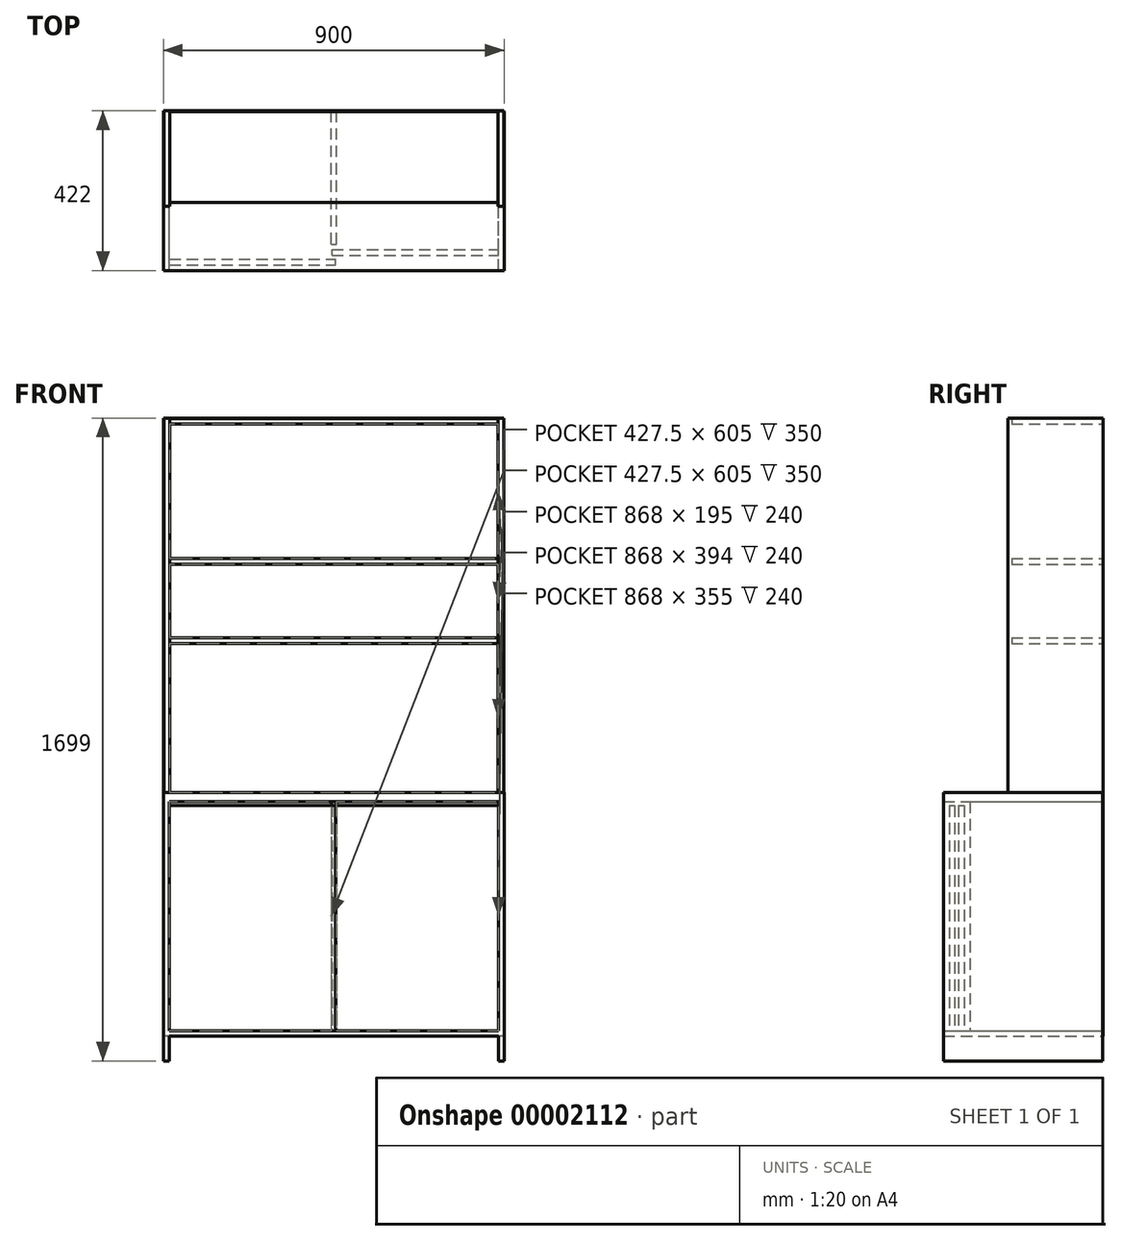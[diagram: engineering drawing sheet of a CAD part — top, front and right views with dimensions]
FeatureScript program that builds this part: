
annotation { "Feature Type Name" : "Feature", "Feature Type Description" : "" }
export const myFeature = defineFeature(function(context is Context, id is Id, definition is map)
    precondition{}
    {
        {
            var Q0;
            Q0=qCreatedBy(makeId("Top.planeOp"),FACE);
            var sketch = newSketch(context, id + "F0", { "sketchPlane" : qUnion([Q0])});
            skLineSegment(sketch, "E0.bottom", {"start": v(0, 0) * mm, "end": v(900, 0) * mm});
            skLineSegment(sketch, "E0.top", {"start": v(0, -420) * mm, "end": v(900, -420) * mm});
            skLineSegment(sketch, "E0.left", {"start": v(0, 0) * mm, "end": v(0, -420) * mm});
            skLineSegment(sketch, "E0.right", {"start": v(900, 0) * mm, "end": v(900, -420) * mm});
            skSolve(sketch);
        }
        {
            var Q0;
            Q0 = qSketchRegion(id + "F0", true);
            extrude(context, id + "F1", {"entities" : qUnion([Q0]), "flatOperationType" : FlatOperationType.REMOVE, "depth" : 24 * mm, "offsetDistance" : 25 * mm, "domain" : OperationDomain.MODEL});
        }
        {
            var Q0;
            Q0=makeQuery(id+"F1.opExtrude","CAP_FACE",FACE,{"disambiguationData":[OSD([sQuery(id+"F0.wireOp",EDGE,"E0.bottom"),sQuery(id+"F0.wireOp",EDGE,"E0.top"),sQuery(id+"F0.wireOp",EDGE,"E0.left"),sQuery(id+"F0.wireOp",EDGE,"E0.right")])],"isStart":true});
            var sketch = newSketch(context, id + "F2", { "sketchPlane" : qUnion([Q0])});
            skLineSegment(sketch, "E1.bottom", {"start": v(0, 420) * mm, "end": v(15, 420) * mm});
            skLineSegment(sketch, "E1.top", {"start": v(0, 0) * mm, "end": v(15, 0) * mm});
            skLineSegment(sketch, "E1.left", {"start": v(0, 420) * mm, "end": v(0, 0) * mm});
            skLineSegment(sketch, "E1.right", {"start": v(15, 420) * mm, "end": v(15, 0) * mm});
            skLineSegment(sketch, "E2.bottom", {"start": v(900, 420) * mm, "end": v(885, 420) * mm});
            skLineSegment(sketch, "E2.top", {"start": v(900, 0) * mm, "end": v(885, 0) * mm});
            skLineSegment(sketch, "E2.left", {"start": v(900, 420) * mm, "end": v(900, 0) * mm});
            skLineSegment(sketch, "E2.right", {"start": v(885, 420) * mm, "end": v(885, 0) * mm});
            skSolve(sketch);
        }
        {
            var Q0;
            Q0 = qSketchRegion(id + "F2", true);
            extrude(context, id + "F3", {"entities" : qUnion([Q0]), "operationType" : NewBodyOperationType.ADD, "depth" : 685 * mm});
        }
        {
            var Q0;
            Q0=makeQuery(id+"F1.opExtrude","CAP_FACE",FACE,{"disambiguationData":[OSD([sQuery(id+"F0.wireOp",EDGE,"E0.bottom"),sQuery(id+"F0.wireOp",EDGE,"E0.top"),sQuery(id+"F0.wireOp",EDGE,"E0.left"),sQuery(id+"F0.wireOp",EDGE,"E0.right")])],"isStart":false});
            var sketch = newSketch(context, id + "F4", { "sketchPlane" : qUnion([Q0])});
            skLineSegment(sketch, "E3.bottom", {"start": v(1, 0) * mm, "end": v(16, 0) * mm});
            skLineSegment(sketch, "E3.top", {"start": v(1, -250) * mm, "end": v(16, -250) * mm});
            skLineSegment(sketch, "E3.left", {"start": v(1, 0) * mm, "end": v(1, -250) * mm});
            skLineSegment(sketch, "E3.right", {"start": v(16, 0) * mm, "end": v(16, -250) * mm});
            skLineSegment(sketch, "E4.bottom", {"start": v(884, 0) * mm, "end": v(899, 0) * mm});
            skLineSegment(sketch, "E4.top", {"start": v(884, -250) * mm, "end": v(899, -250) * mm});
            skLineSegment(sketch, "E4.left", {"start": v(884, 0) * mm, "end": v(884, -250) * mm});
            skLineSegment(sketch, "E4.right", {"start": v(899, 0) * mm, "end": v(899, -250) * mm});
            skSolve(sketch);
        }
        {
            var Q0;
            Q0 = qSketchRegion(id + "F4", true);
            extrude(context, id + "F5", {"entities" : qUnion([Q0]), "operationType" : NewBodyOperationType.ADD, "depth" : 990 * mm});
        }
        {
            var Q0;
            Q0=makeQuery(id+"F5.opExtrude","SWEPT_FACE",FACE,{"disambiguationData":[OSD([sQuery(id+"F4.wireOp",EDGE,"E3.right")])]});
            var sketch = newSketch(context, id + "F6", { "sketchPlane" : qUnion([Q0])});
            skLineSegment(sketch, "E5.bottom", {"start": v(-240, 1013) * mm, "end": v(0, 1013) * mm});
            skLineSegment(sketch, "E5.top", {"start": v(-240, 998) * mm, "end": v(0, 998) * mm});
            skLineSegment(sketch, "E5.left", {"start": v(-240, 1013) * mm, "end": v(-240, 998) * mm});
            skLineSegment(sketch, "E5.right", {"start": v(0, 1013) * mm, "end": v(0, 998) * mm});
            skLineSegment(sketch, "E6.bottom", {"start": v(-240, 643) * mm, "end": v(0, 643) * mm});
            skLineSegment(sketch, "E6.top", {"start": v(-240, 628) * mm, "end": v(0, 628) * mm});
            skLineSegment(sketch, "E6.left", {"start": v(-240, 643) * mm, "end": v(-240, 628) * mm});
            skLineSegment(sketch, "E6.right", {"start": v(0, 643) * mm, "end": v(0, 628) * mm});
            skLineSegment(sketch, "E7.bottom", {"start": v(-240, 433) * mm, "end": v(0, 433) * mm});
            skLineSegment(sketch, "E7.top", {"start": v(-240, 418) * mm, "end": v(0, 418) * mm});
            skLineSegment(sketch, "E7.left", {"start": v(-240, 433) * mm, "end": v(-240, 418) * mm});
            skLineSegment(sketch, "E7.right", {"start": v(0, 433) * mm, "end": v(0, 418) * mm});
            skSolve(sketch);
        }
        {
            var Q0;
            Q0 = qSketchRegion(id + "F6", true);
            extrude(context, id + "F7", {"entities" : qUnion([Q0]), "operationType" : NewBodyOperationType.ADD, "endBound" : BoundingType.UP_TO_NEXT, "depth" : 873.45 * mm});
        }
        {
            var Q0;
            Q0=makeQuery(id+"F3.opExtrude","SWEPT_FACE",FACE,{"disambiguationData":[OSD([sQuery(id+"F2.wireOp",EDGE,"E1.right")])]});
            var sketch = newSketch(context, id + "F8", { "sketchPlane" : qUnion([Q0])});
            skLineSegment(sketch, "E8.bottom", {"start": v(-420, -620) * mm, "end": v(0, -620) * mm});
            skLineSegment(sketch, "E8.top", {"start": v(-420, -605) * mm, "end": v(0, -605) * mm});
            skLineSegment(sketch, "E8.left", {"start": v(-420, -620) * mm, "end": v(-420, -605) * mm});
            skLineSegment(sketch, "E8.right", {"start": v(0, -620) * mm, "end": v(0, -605) * mm});
            skSolve(sketch);
        }
        {
            var Q0;
            Q0 = qSketchRegion(id + "F8", true);
            extrude(context, id + "F9", {"entities" : qUnion([Q0]), "operationType" : NewBodyOperationType.ADD, "endBound" : BoundingType.UP_TO_NEXT, "depth" : 25 * mm});
        }
        {
            var Q0;
            Q0=makeQuery(id+"F9.opExtrude","SWEPT_FACE",FACE,{"disambiguationData":[OSD([sQuery(id+"F8.wireOp",EDGE,"E8.top")])]});
            var sketch = newSketch(context, id + "F10", { "sketchPlane" : qUnion([Q0])});
            skLineSegment(sketch, "E9.bottom", {"start": v(442.5, -350) * mm, "end": v(457.5, -350) * mm});
            skLineSegment(sketch, "E9.top", {"start": v(442.5, 0) * mm, "end": v(457.5, 0) * mm});
            skLineSegment(sketch, "E9.left", {"start": v(442.5, -350) * mm, "end": v(442.5, 0) * mm});
            skLineSegment(sketch, "E9.right", {"start": v(457.5, -350) * mm, "end": v(457.5, 0) * mm});
            skSolve(sketch);
        }
        {
            var Q0;
            Q0 = qSketchRegion(id + "F10", true);
            extrude(context, id + "F11", {"entities" : qUnion([Q0]), "operationType" : NewBodyOperationType.ADD, "endBound" : BoundingType.UP_TO_NEXT, "depth" : 25 * mm});
        }
        {
            var Q0;
            Q0=makeQuery(id+"F11.boolean.opBoolean","MERGE",FACE,{"derivedFrom":[makeQuery(id+"F9.boolean.opBoolean","MERGE",FACE,{"derivedFrom":[makeQuery(id+"F7.boolean.opBoolean","MERGE",FACE,{"derivedFrom":[makeQuery(id+"F5.boolean.opBoolean","MERGE",FACE,{"derivedFrom":[makeQuery(id+"F3.boolean.opBoolean","MERGE",FACE,{"derivedFrom":[makeQuery(id+"F1.opExtrude","SWEPT_FACE",FACE,{"disambiguationData":[OSD([sQuery(id+"F0.wireOp",EDGE,"E0.bottom")])]}),makeQuery(id+"F3.opExtrude","SWEPT_FACE",FACE,{"disambiguationData":[OSD([sQuery(id+"F2.wireOp",EDGE,"E1.top")])]}),makeQuery(id+"F3.opExtrude","SWEPT_FACE",FACE,{"disambiguationData":[OSD([sQuery(id+"F2.wireOp",EDGE,"E2.top")])]})]}),makeQuery(id+"F5.opExtrude","SWEPT_FACE",FACE,{"disambiguationData":[OSD([sQuery(id+"F4.wireOp",EDGE,"E3.bottom")])]}),makeQuery(id+"F5.opExtrude","SWEPT_FACE",FACE,{"disambiguationData":[OSD([sQuery(id+"F4.wireOp",EDGE,"E4.bottom")])]})]}),makeQuery(id+"F7.opExtrude","SWEPT_FACE",FACE,{"disambiguationData":[OSD([sQuery(id+"F6.wireOp",EDGE,"E5.right")])]}),makeQuery(id+"F7.opExtrude","SWEPT_FACE",FACE,{"disambiguationData":[OSD([sQuery(id+"F6.wireOp",EDGE,"E6.right")])]}),makeQuery(id+"F7.opExtrude","SWEPT_FACE",FACE,{"disambiguationData":[OSD([sQuery(id+"F6.wireOp",EDGE,"E7.right")])]})]}),makeQuery(id+"F9.opExtrude","SWEPT_FACE",FACE,{"disambiguationData":[OSD([sQuery(id+"F8.wireOp",EDGE,"E8.right")])]})]}),makeQuery(id+"F11.opExtrude","SWEPT_FACE",FACE,{"disambiguationData":[OSD([sQuery(id+"F10.wireOp",EDGE,"E9.top")])]})]});
            var sketch = newSketch(context, id + "F12", { "sketchPlane" : qUnion([Q0])});
            skLineSegment(sketch, "E10.bottom", {"start": v(-899, 1014) * mm, "end": v(0, 1014) * mm});
            skLineSegment(sketch, "E10.top", {"start": v(-899, -620) * mm, "end": v(0, -620) * mm});
            skLineSegment(sketch, "E10.left", {"start": v(-899, 1014) * mm, "end": v(-899, -620) * mm});
            skLineSegment(sketch, "E10.right", {"start": v(0, 1014) * mm, "end": v(0, -620) * mm});
            skSolve(sketch);
        }
        {
            var Q0;
            Q0 = qSketchRegion(id + "F12", true);
            extrude(context, id + "F13", {"entities" : qUnion([Q0]), "operationType" : NewBodyOperationType.ADD, "depth" : 2 * mm});
        }
        {
            var Q0;
            Q0=makeQuery(id+"F9.opExtrude","SWEPT_FACE",FACE,{"disambiguationData":[OSD([sQuery(id+"F8.wireOp",EDGE,"E8.top")])]});
            var sketch = newSketch(context, id + "F14", { "sketchPlane" : qUnion([Q0])});
            skLineSegment(sketch, "E11.bottom", {"start": v(15, -405) * mm, "end": v(455, -405) * mm});
            skLineSegment(sketch, "E11.top", {"start": v(15, -390) * mm, "end": v(455, -390) * mm});
            skLineSegment(sketch, "E11.left", {"start": v(15, -405) * mm, "end": v(15, -390) * mm});
            skLineSegment(sketch, "E11.right", {"start": v(455, -405) * mm, "end": v(455, -390) * mm});
            skLineSegment(sketch, "E12.bottom", {"start": v(445, -380) * mm, "end": v(885, -380) * mm});
            skLineSegment(sketch, "E12.top", {"start": v(445, -365) * mm, "end": v(885, -365) * mm});
            skLineSegment(sketch, "E12.left", {"start": v(445, -380) * mm, "end": v(445, -365) * mm});
            skLineSegment(sketch, "E12.right", {"start": v(885, -380) * mm, "end": v(885, -365) * mm});
            skSolve(sketch);
        }
        {
            var Q0;
            Q0 = qSketchRegion(id + "F14", true);
            extrude(context, id + "F15", {"entities" : qUnion([Q0]), "operationType" : NewBodyOperationType.ADD, "depth" : 595 * mm});
        }
    });
